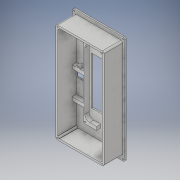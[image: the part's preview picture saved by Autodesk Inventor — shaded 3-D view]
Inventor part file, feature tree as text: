
AUTODESK INVENTOR PART (.ipt)
format: ipt  version: 2019 (Build 230136000, 136)  size: 309,760 bytes
history: native  units: in
note: dims shown in document units (in); Inventor stores cm internally (conversion verified against a paired STEP export)
features: sketch x7, extrude x5, hole x3, projected_geometry x2, fillet x1
ambient origin geometry x8: Origin, YZ Plane, XZ Plane, XY Plane, X Axis, Y Axis, Z Axis, Center Point
bodies: Solid1 (feature_tree)
feature tree (18):
  extrude  "Border"  Depth=0.1in TaperAngle=0.0deg
  extrude  "Screen Cutouts"  Depth=1.75in
  extrude  "Outer Frame"  Depth=1.75in
  extrude  "Electronic Frame"  Depth=0.125in
  hole  "Electronic Mounting Holes"  [1 undecoded]
  hole  "FrameMounting Holes"  [1 undecoded]
  extrude  "ButtonChargerCutout"  Depth=0.35in
  hole  "Outer Holes"  [1 undecoded]
  fillet  "Frame Fillet"  Radius=0.143in
  sketch  "Sketch1"  dims[d3=0.1in d4=0.0in d29=1.0in d30=0.0in]
  sketch  "Sketch5"  dims[d33=1.75in d34=0.315in]
  sketch  "Sketch6"  dims[d35=0.315in d36=1.75in]
  projected_geometry  "Projected Loop3"
  sketch  "Sketch7"  dims[d39=0.143in d40=0.125in]
  sketch  "Sketch10"  dims[d41=0.125in d42=1.373in d43=0.0in]
  sketch  "Sketch11"  dims[d45=2.33in d46=4.9in]
  projected_geometry  "Projected Loop4"
  sketch  "Sketch13"  dims[d47=0.1in d53=0.35in d54=0.31in d55=0.0in d56=0.143in d60=0.0017in d61=0.25in d62=0.125in d63=0.125in d64=0.125in d65=0.125in d76=0.1in d77=0.75in d78=0.375in d79=0.25in d80=0.5635in d81=0.35in d82=0.8108in d96=0.1in d97=0.75in d98=0.375in d99=0.25in d100=0.5635in d101=0.33in d102=0.8108in d105=0.125in d111=0.51in d112=0.31in d113=0.0in d114=0.125in d115=0.125in d116=0.125in d117=0.125in d118=0.1in d119=0.75in d120=0.375in d121=0.25in d122=0.5635in d123=1.0in d124=0.8108in d126=0.125in d127=0.3in d128=0.06in]
note: 3 required parameter values undecoded (feature->parameter linkage not recoverable at this tier; creation-order binding heuristic only, values carry confidence <= 0.55)
